# Revit family: LAMP_KOMBIC 100 SQUARE IP40 CRI80 OPTIC
name_source: partatom
category: Luminarias
revit_build: Autodesk Revit 2018 (Build: 20190510_1515(x64)
units: mm (PartAtom-declared; Revit-internal decimal feet)

## family parameters
Anfitrión = Cara
Compartido = No
Corte con vacíos al cargar = No
Cota de conector redondo = Diámetro de uso
Origen de luz = Sí
Punto de cálculo de habitación = No
Tipo de pieza = Normal

## types (16) — shared parameters
CRI = 80
Cambio de temperatura de color de luz atenuada = <Ninguno>
Dimensions = 99x99x75
Elevación por defecto = 1219 mm
Fabricante = LAMP
Filtro de color = 16777215
Gear = Electronic
Height = 75 mm
IEE = A+
Installation instructions = https://www.lamp.es
Insulation class = II
Lamp = COB LED
Last update = 19/07/2021
Luminaire type = Downlight
MacAdam = 3
Manufacturer URL = http://www.lamp.es
Manufacturer country = Spain
Manufacturer name = LAMP
Material COB = LAMP_COB
Material difusor = LAMP_PMMA Difusor Kombic
Material disipador = LAMP_Aluminio Disipador Kombic
Material optica = LAMP_PMMA Optica Kombic100
Power Supply = 220-240V 50/60Hz
Product URL = https://www.lamp.es
Product datasheet = http://www.lamp.es
Protection rating = IP40
Recessed dimensions = 95x95
Type = COB PHILIPS
Weight = 0.38 kg
Ángulo de inclinación = -90.00°

## per-type parameters (varying)
| type | Archivo de red fotométrica | Efficacy | Finish | LED Lifetime | Material aro | Material reflector | Modelo | Plum | Power | Product code | UGR |
| 1264LM 3000K  BK/BK | K11SQ2040WF830NBB.IES | 92 lm/W | Matte black RAL 9011 | 50.000 L80 B10 | LAMP_Plástico genérico NG | LAMP_PC Reflector Kombic Metalizado Negro | K11SQ2040WF830NBB | 14 W | 12 W | K11SQ2040WF830NBB | 17 |
| 1264LM 3000K  BK/W | K11SQ2040WF830NBW.IES | 92 lm/W | Shiny white RAL 9010 | 50.000 L80 B10 | LAMP_Plástico genérico BL | LAMP_PC Reflector Kombic Metalizado Negro | K11SQ2040WF830NBW | 14 W | 12 W | K11SQ2040WF830NBW | 17 |
| 1298LM 3000K  M/W | K11SQ2040WF830NMW.IES | 95 lm/W | Shiny white RAL 9010 | 50.000 L80 B10 | LAMP_Plástico genérico BL | LAMP_PC Reflector Kombic Metalizado Mate | K11SQ2040WF830NMW | 14 W | 12 W | K11SQ2040WF830NMW | 17 |
| 1306LM 3000K  W/W | K11SQ2040WF830NWW.IES | 95 lm/W | Matte white RAL 9010 | 50.000 L80 B10 | LAMP_Plástico genérico BL | LAMP_PC Reflector Kombic Blanco | K11SQ2040WF830NWW | 14 W | 12 W | K11SQ2040WF830NWW | 19 |
| 1339LM 4000K  BK/BK | K11SQ2040WF840NBB.IES | 98 lm/W | Matte black RAL 9011 | 50.000 L80 B10 | LAMP_Plástico genérico NG | LAMP_PC Reflector Kombic Metalizado Negro | K11SQ2040WF840NBB | 14 W | 12 W | K11SQ2040WF840NBB | 17 |
| 1339LM 4000K  BK/W | K11SQ2040WF840NBW.IES | 98 lm/W | Shiny white RAL 9010 | 50.000 L80 B10 | LAMP_Plástico genérico BL | LAMP_PC Reflector Kombic Metalizado Negro | K11SQ2040WF840NBW | 14 W | 12 W | K11SQ2040WF840NBW | 17 |
| 1375LM 4000K  M/W | K11SQ2040WF840NMW.IES | 100 lm/W | Shiny white RAL 9010 | 50.000 L80 B10 | LAMP_Plástico genérico BL | LAMP_PC Reflector Kombic Metalizado Mate | K11SQ2040WF840NMW | 14 W | 12 W | K11SQ2040WF840NMW | 17 |
| 1383LM 4000K  W/W | K11SQ2040WF840NWW.IES | 101 lm/W | Matte white RAL 9010 | 50.000 L80 B10 | LAMP_Plástico genérico BL | LAMP_PC Reflector Kombic Blanco | K11SQ2040WF840NWW | 14 W | 12 W | K11SQ2040WF840NWW | 19 |
| 1686LM 3000K  BK/BK | K11SQ2540WF830NBB.IES | 85 lm/W | Matte black RAL 9011 | 50.000 L70 B10 | LAMP_Plástico genérico NG | LAMP_PC Reflector Kombic Metalizado Negro | K11SQ2540WF830NBB | 20 W | 18 W | K11SQ2540WF830NBB | 17 |
| 1686LM 3000K  BK/W | K11SQ2540WF830NBW.IES | 85 lm/W | Shiny white RAL 9010 | 50.000 L70 B10 | LAMP_Plástico genérico BL | LAMP_PC Reflector Kombic Metalizado Negro | K11SQ2540WF830NBW | 20 W | 18 W | K11SQ2540WF830NBW | 17 |
| 1731LM 3000K  M/W | K11SQ2540WF830NMW.IES | 87 lm/W | Shiny white RAL 9010 | 50.000 L70 B10 | LAMP_Plástico genérico BL | LAMP_PC Reflector Kombic Metalizado Mate | K11SQ2540WF830NMW | 20 W | 18 W | K11SQ2540WF830NMW | 17 |
| 1742LM 3000K  W/W | K11SQ2540WF830NWW.IES | 88 lm/W | Matte white RAL 9010 | 50.000 L70 B10 | LAMP_Plástico genérico BL | LAMP_PC Reflector Kombic Blanco | K11SQ2540WF830NWW | 20 W | 18 W | K11SQ2540WF830NWW | 19 |
| 1786LM 4000K  BK/BK | K11SQ2540WF840NBB.IES | 90 lm/W | Matte black RAL 9011 | 50.000 L70 B10 | LAMP_Plástico genérico NG | LAMP_PC Reflector Kombic Metalizado Negro | K11SQ2540WF840NBB | 20 W | 18 W | K11SQ2540WF840NBB | 17 |
| 1786LM 4000K  BK/W | K11SQ2540WF840NBW.IES | 90 lm/W | Shiny white RAL 9010 | 50.000 L70 B10 | LAMP_Plástico genérico BL | LAMP_PC Reflector Kombic Metalizado Negro | K11SQ2540WF840NBW | 20 W | 18 W | K11SQ2540WF840NBW | 17 |
| 1834LM 4000K  M/W | K11SQ2540WF840NMW.IES | 93 lm/W | Shiny white RAL 9010 | 50.000 L70 B10 | LAMP_Plástico genérico BL | LAMP_PC Reflector Kombic Metalizado Mate | K11SQ2540WF840NMW | 20 W | 18 W | K11SQ2540WF840NMW | 17 |
| 1845LM 4000K  W/W | K11SQ2540WF840NWW.IES | 93 lm/W | Matte white RAL 9010 | 50.000 L70 B10 | LAMP_Plástico genérico BL | LAMP_PC Reflector Kombic Blanco | K11SQ2540WF840NWW | 20 W | 18 W | K11SQ2540WF840NWW | 19 |
